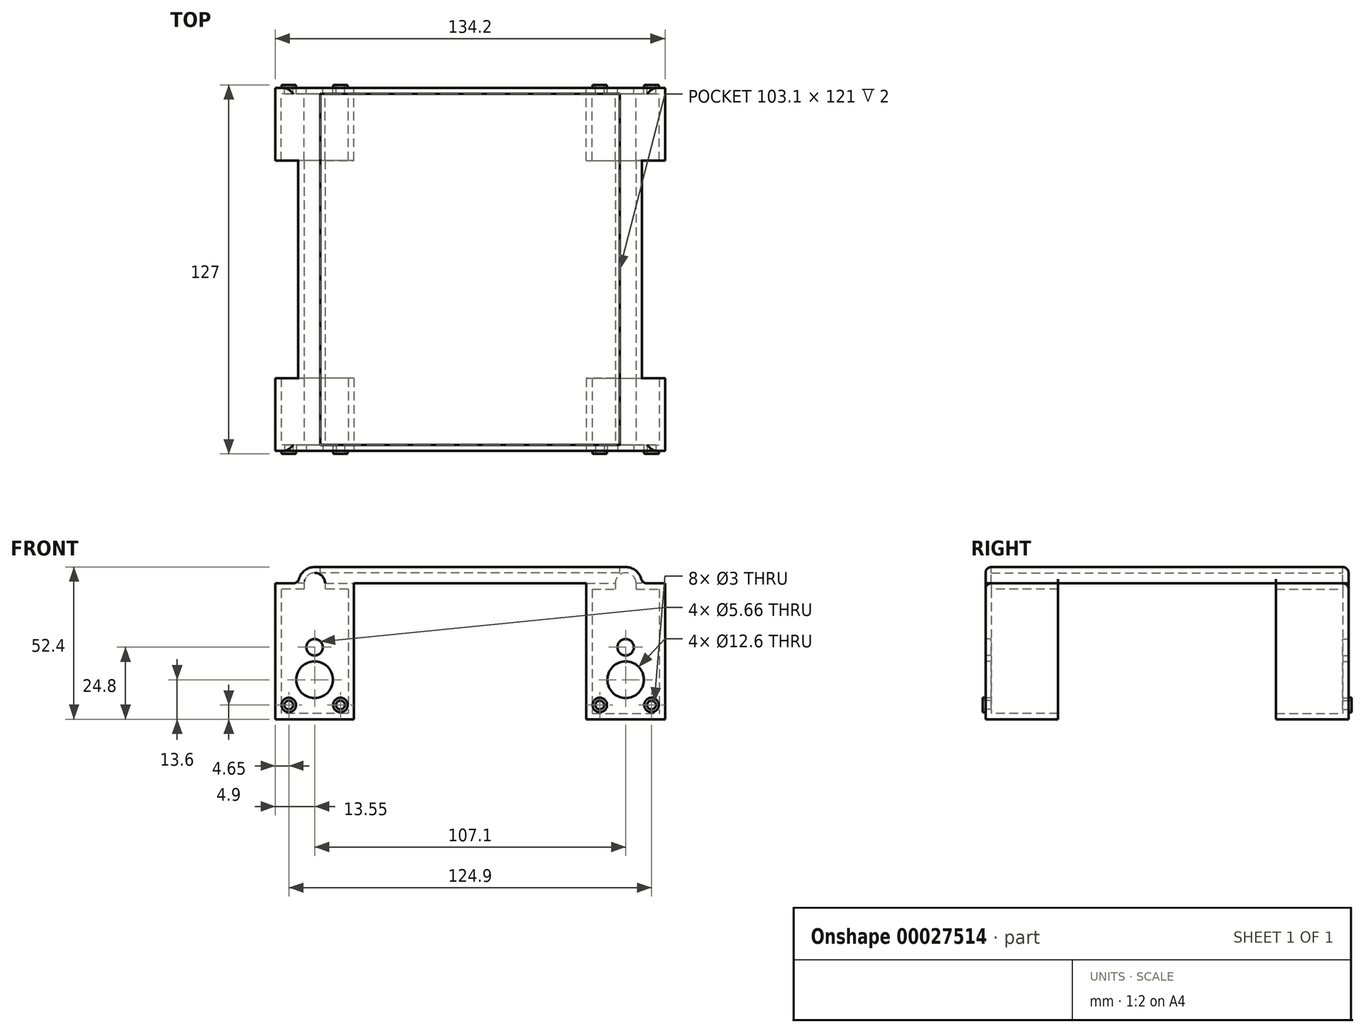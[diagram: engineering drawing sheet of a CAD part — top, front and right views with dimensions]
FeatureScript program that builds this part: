
annotation { "Feature Type Name" : "Feature", "Feature Type Description" : "" }
export const myFeature = defineFeature(function(context is Context, id is Id, definition is map)
    precondition{}
    {
        {
            assignVariable(context, id + "F0", {"name" : "FrameThickness", "anyValue" : 2});
        }
        {
            var Q0;
            Q0=qCreatedBy(makeId("Front.planeOp"),FACE);
            var sketch = newSketch(context, id + "F1", { "sketchPlane" : qUnion([Q0])});
            skLineSegment(sketch, "E0.rect.bottom", {"start": v(11.55, 21.4) * mm, "end": v(3.6, 21.4) * mm});
            skLineSegment(sketch, "E0.rect.top", {"start": v(11.55, -21.4) * mm, "end": v(-11.55, -21.4) * mm});
            skLineSegment(sketch, "E0.rect.left", {"start": v(11.55, 21.4) * mm, "end": v(11.55, -21.4) * mm});
            skLineSegment(sketch, "E0.rect.right", {"start": v(-11.55, 21.4) * mm, "end": v(-11.55, -21.4) * mm});
            skPoint(sketch, "E0.rect.middle", {"position": v(0, 0) * mm});
            skLineSegment(sketch, "E1.0", {"start": v(13.55, 23.4) * mm, "end": v(5.6, 23.4) * mm});
            skLineSegment(sketch, "E1.1", {"start": v(13.55, 23.4) * mm, "end": v(13.55, -23.4) * mm});
            skLineSegment(sketch, "E1.2", {"start": v(13.55, -23.4) * mm, "end": v(-13.55, -23.4) * mm});
            skLineSegment(sketch, "E1.3", {"start": v(-13.55, 23.4) * mm, "end": v(-13.55, -23.4) * mm});
            skCircle(sketch, "E2", {"center": v(0, -9.8) * mm, "radius": 6.3 * mm});
            skPoint(sketch, "E2.centerSnap0", {"position": v(0, -21.4) * mm});
            skLineSegment(sketch, "E3", {"start": v(0, -9.8) * mm, "end": v(0, -21.4) * mm, "construction": true});
            skCircle(sketch, "E4", {"center": v(8.9, -18.5) * mm, "radius": 1.5 * mm});
            skCircle(sketch, "E5", {"center": v(-8.9, -18.5) * mm, "radius": 1.5 * mm});
            skCircle(sketch, "E6", {"center": v(0, 1.4) * mm, "radius": 2.83 * mm});
            skLineSegment(sketch, "E7", {"start": v(0, 1.4) * mm, "end": v(0, -9.8) * mm, "construction": true});
            skLineSegment(sketch, "E8", {"start": v(-11.55, -9.8) * mm, "end": v(11.55, -9.8) * mm, "construction": true});
            skLineSegment(sketch, "E9", {"start": v(8.9, -18.5) * mm, "end": v(8.9, -9.8) * mm, "construction": true});
            skLineSegment(sketch, "E10", {"start": v(8.9, -18.5) * mm, "end": v(-8.9, -18.5) * mm, "construction": true});
            skArc(sketch, "E11", {"start": v(3.6, 23.4) * mm, "mid": v(0, 27) * mm, "end": v(-3.6, 23.4) * mm});
            skLineSegment(sketch, "E12", {"start": v(3.6, 23.4) * mm, "end": v(-3.6, 23.4) * mm, "construction": true});
            skLineSegment(sketch, "E13", {"start": v(0, 23.4) * mm, "end": v(0, 27) * mm, "construction": true});
            skArc(sketch, "E14.0", {"start": v(5.6, 23.4) * mm, "mid": v(3.96, 27.36) * mm, "end": v(0, 29) * mm, "construction": true});
            skLineSegment(sketch, "E15", {"start": v(-5.6, 23.4) * mm, "end": v(-13.55, 23.4) * mm});
            skLineSegment(sketch, "E16", {"start": v(-3.6, 23.4) * mm, "end": v(-3.6, 21.4) * mm});
            skLineSegment(sketch, "E17", {"start": v(3.6, 23.4) * mm, "end": v(3.6, 21.4) * mm});
            skLineSegment(sketch, "E18", {"start": v(-3.6, 21.4) * mm, "end": v(-11.55, 21.4) * mm});
            skLineSegment(sketch, "E19", {"start": v(3.6, 21.4) * mm, "end": v(-3.6, 21.4) * mm});
            skCircle(sketch, "E20.0", {"center": v(8.9, -18.5) * mm, "radius": 2.5 * mm});
            skLineSegment(sketch, "E21.0", {"start": v(8.9, -13.5) * mm, "end": v(-8.9, -13.5) * mm});
            skCircle(sketch, "E22.0", {"center": v(-8.9, -18.5) * mm, "radius": 2.5 * mm});
            skLineSegment(sketch, "E23", {"start": v(5.6, 23.4) * mm, "end": v(5.6, 29) * mm});
            skPoint(sketch, "E23.endSnap0", {"position": v(0, 29) * mm});
            skLineSegment(sketch, "E24", {"start": v(5.6, 29) * mm, "end": v(0, 29) * mm});
            skArc(sketch, "E25", {"start": v(0, 29) * mm, "mid": v(-3.96, 27.36) * mm, "end": v(-5.6, 23.4) * mm});
            skSolve(sketch);
        }
        {
            var Q0;
            Q0=makeQuery(id+"F1.imprint","IMPRINT",FACE,{"disambiguationData":[TD([[makeQuery(id+"F1.imprint","IMPRINT",EDGE,{"derivedFrom":sQuery(id+"F1.wireOp",EDGE,"E0.rect.bottom")}),1.0]])]});
            var Q1;
            Q1=makeQuery(id+"F1.imprint","IMPRINT",FACE,{"disambiguationData":[TD([[makeQuery(id+"F1.imprint","IMPRINT",EDGE,{"derivedFrom":sQuery(id+"F1.wireOp",EDGE,"E11")}),1.0]])]});
            var Q2;
            Q2=makeQuery(id+"F1.imprint","IMPRINT",FACE,{"disambiguationData":[TD([[makeQuery(id+"F1.imprint","IMPRINT",EDGE,{"derivedFrom":sQuery(id+"F1.wireOp",EDGE,"E5")}),-1.0]])]});
            var Q3;
            Q3=makeQuery(id+"F1.imprint","IMPRINT",FACE,{"disambiguationData":[TD([[makeQuery(id+"F1.imprint","IMPRINT",EDGE,{"derivedFrom":sQuery(id+"F1.wireOp",EDGE,"E4")}),-1.0]])]});
            extrude(context, id + "F2", {"entities" : qUnion([Q0, Q1, Q2, Q3]), "depth" : (getVariable(context, 'FrameThickness')) * mm});
        }
        {
            var Q0;
            Q0=makeQuery(id+"F1.imprint","IMPRINT",FACE,{"disambiguationData":[TD([[makeQuery(id+"F1.imprint","IMPRINT",EDGE,{"derivedFrom":sQuery(id+"F1.wireOp",EDGE,"E5")}),-1.0]])]});
            var Q1;
            Q1=makeQuery(id+"F1.imprint","IMPRINT",FACE,{"disambiguationData":[TD([[makeQuery(id+"F1.imprint","IMPRINT",EDGE,{"derivedFrom":sQuery(id+"F1.wireOp",EDGE,"E4")}),-1.0]])]});
            extrude(context, id + "F3", {"entities" : qUnion([Q0, Q1]), "operationType" : NewBodyOperationType.ADD, "oppositeDirection" : true, "depth" : 1 * mm});
        }
        {
            var Q0;
            Q0=makeQuery(id+"F1.imprint","IMPRINT",FACE,{"disambiguationData":[TD([[makeQuery(id+"F1.imprint","IMPRINT",EDGE,{"derivedFrom":sQuery(id+"F1.wireOp",EDGE,"E0.rect.bottom")}),-1.0]])]});
            extrude(context, id + "F4", {"entities" : qUnion([Q0]), "operationType" : NewBodyOperationType.ADD, "depth" : 25 * mm});
        }
        {
            var Q0;
            {var subQ0=sQuery(id+"F1.wireOp",EDGE,"E1.0");var subQ1=sQuery(id+"F1.wireOp",EDGE,"E23");var subQ2=makeQuery(id+"F4.opExtrude","CAP_VERTEX",VERTEX,{"disambiguationData":[OSD([subQ0,subQ1])],"isStart":true});Q0=makeQuery(id+"F11.opLoft","SWEPT_EDGE",EDGE,{"disambiguationData":[OSD([subQ0,subQ1]),TDD([subQ2,makeQuery(id+"F8.opPattern","COPY",VERTEX,{"derivedFrom":subQ2,"instanceName":"1"})])]});}
            var Q1;
            {var subQ0=sQuery(id+"F1.wireOp",EDGE,"E24");var subQ1=makeQuery(id+"F4.opExtrude","CAP_EDGE",EDGE,{"disambiguationData":[OSD([subQ0])],"isStart":true});var subQ2=sQuery(id+"F1.wireOp",EDGE,"E23");var subQ3=makeQuery(id+"F4.opExtrude","CAP_VERTEX",VERTEX,{"disambiguationData":[OSD([subQ2,subQ0])],"isStart":true});Q1=makeQuery(id+"F11.boolean.opBoolean","MERGE",EDGE,{"derivedFrom":[subQ1,makeQuery(id+"F8.opPattern","COPY",EDGE,{"derivedFrom":subQ1,"instanceName":"1"}),makeQuery(id+"F11.opLoft","SWEPT_EDGE",EDGE,{"disambiguationData":[OSD([subQ2,subQ0]),TDD([subQ3,makeQuery(id+"F8.opPattern","COPY",VERTEX,{"derivedFrom":subQ3,"instanceName":"1"})])]})]});}
            var Q2;
            Q2=makeQuery(id+"F8.opPattern","COPY",EDGE,{"derivedFrom":makeQuery(id+"F4.opExtrude","SWEPT_EDGE",EDGE,{"disambiguationData":[OSD([sQuery(id+"F1.wireOp",EDGE,"E15"),sQuery(id+"F1.wireOp",EDGE,"E25")])]}),"instanceName":"1"});
            var Q3;
            Q3=makeQuery(id+"F8.opPattern","COPY",EDGE,{"derivedFrom":makeQuery(id+"F6.opPattern","COPY",EDGE,{"derivedFrom":makeQuery(id+"F4.opExtrude","SWEPT_EDGE",EDGE,{"disambiguationData":[OSD([sQuery(id+"F1.wireOp",EDGE,"E15"),sQuery(id+"F1.wireOp",EDGE,"E25")])]}),"instanceName":"1"}),"instanceName":"1"});
            var Q4;
            {var subQ0=sQuery(id+"F1.wireOp",EDGE,"E1.0");var subQ1=sQuery(id+"F1.wireOp",EDGE,"E23");var subQ2=makeQuery(id+"F6.opPattern","COPY",VERTEX,{"derivedFrom":makeQuery(id+"F4.opExtrude","CAP_VERTEX",VERTEX,{"disambiguationData":[OSD([subQ0,subQ1])],"isStart":true}),"instanceName":"1"});Q4=makeQuery(id+"F10.opLoft","SWEPT_EDGE",EDGE,{"disambiguationData":[OSD([subQ0,subQ1]),TDD([subQ2,makeQuery(id+"F8.opPattern","COPY",VERTEX,{"derivedFrom":subQ2,"instanceName":"1"})])]});}
            var Q5;
            {var subQ0=sQuery(id+"F1.wireOp",EDGE,"E24");var subQ1=makeQuery(id+"F6.opPattern","COPY",EDGE,{"derivedFrom":makeQuery(id+"F4.opExtrude","CAP_EDGE",EDGE,{"disambiguationData":[OSD([subQ0])],"isStart":true}),"instanceName":"1"});var subQ2=sQuery(id+"F1.wireOp",EDGE,"E23");var subQ3=makeQuery(id+"F6.opPattern","COPY",VERTEX,{"derivedFrom":makeQuery(id+"F4.opExtrude","CAP_VERTEX",VERTEX,{"disambiguationData":[OSD([subQ2,subQ0])],"isStart":true}),"instanceName":"1"});Q5=makeQuery(id+"F10.boolean.opBoolean","MERGE",EDGE,{"derivedFrom":[subQ1,makeQuery(id+"F8.opPattern","COPY",EDGE,{"derivedFrom":subQ1,"instanceName":"1"}),makeQuery(id+"F10.opLoft","SWEPT_EDGE",EDGE,{"disambiguationData":[OSD([subQ2,subQ0]),TDD([subQ3,makeQuery(id+"F8.opPattern","COPY",VERTEX,{"derivedFrom":subQ3,"instanceName":"1"})])]})]});}
            var Q6;
            Q6=makeQuery(id+"F6.opPattern","COPY",EDGE,{"derivedFrom":makeQuery(id+"F4.opExtrude","SWEPT_EDGE",EDGE,{"disambiguationData":[OSD([sQuery(id+"F1.wireOp",EDGE,"E15"),sQuery(id+"F1.wireOp",EDGE,"E25")])]}),"instanceName":"1"});
            var Q7;
            Q7=makeQuery(id+"F4.opExtrude","SWEPT_EDGE",EDGE,{"disambiguationData":[OSD([sQuery(id+"F1.wireOp",EDGE,"E15"),sQuery(id+"F1.wireOp",EDGE,"E25")])]});
            fillet(context, id + "F5", {"entities" : qUnion([Q0, Q1, Q2, Q3, Q4, Q5, Q6, Q7]), "radius" : 2 * mm, "tangentPropagation" : true, "allowEdgeOverflow" : false});
        }
        {
            var Q0;
            Q0=makeQuery(id+"F2.opExtrude","SWEPT_BODY",BODY,{"disambiguationData":[OSD([sQuery(id+"F1.wireOp",EDGE,"E0.rect.bottom"),sQuery(id+"F1.wireOp",EDGE,"E0.rect.top"),sQuery(id+"F1.wireOp",EDGE,"E0.rect.left"),sQuery(id+"F1.wireOp",EDGE,"E0.rect.right"),sQuery(id+"F1.wireOp",EDGE,"E2"),sQuery(id+"F1.wireOp",EDGE,"E4"),sQuery(id+"F1.wireOp",EDGE,"E5"),sQuery(id+"F1.wireOp",EDGE,"E6"),sQuery(id+"F1.wireOp",EDGE,"E11"),sQuery(id+"F1.wireOp",EDGE,"E16"),sQuery(id+"F1.wireOp",EDGE,"E17"),sQuery(id+"F1.wireOp",EDGE,"E18")])]});
            var Q1;
            Q1=makeQuery(id+"F4.opExtrude","CAP_FACE",FACE,{"disambiguationData":[OSD([sQuery(id+"F1.wireOp",EDGE,"E0.rect.bottom"),sQuery(id+"F1.wireOp",EDGE,"E0.rect.top"),sQuery(id+"F1.wireOp",EDGE,"E0.rect.left"),sQuery(id+"F1.wireOp",EDGE,"E0.rect.right"),sQuery(id+"F1.wireOp",EDGE,"E1.0"),sQuery(id+"F1.wireOp",EDGE,"E1.1"),sQuery(id+"F1.wireOp",EDGE,"E1.2"),sQuery(id+"F1.wireOp",EDGE,"E1.3"),sQuery(id+"F1.wireOp",EDGE,"E11"),sQuery(id+"F1.wireOp",EDGE,"E14.0"),sQuery(id+"F1.wireOp",EDGE,"E15"),sQuery(id+"F1.wireOp",EDGE,"E16"),sQuery(id+"F1.wireOp",EDGE,"E17"),sQuery(id+"F1.wireOp",EDGE,"E18")])],"isStart":false});
            mirror(context, id + "F6", {"entities" : qUnion([Q0]), "mirrorPlane" : qUnion([Q1])});
        }
        {
            var Q0;
            Q0=makeQuery(id+"F6.opPattern","COPY",BODY,{"derivedFrom":makeQuery(id+"F2.opExtrude","SWEPT_BODY",BODY,{"disambiguationData":[OSD([sQuery(id+"F1.wireOp",EDGE,"E0.rect.bottom"),sQuery(id+"F1.wireOp",EDGE,"E0.rect.top"),sQuery(id+"F1.wireOp",EDGE,"E0.rect.left"),sQuery(id+"F1.wireOp",EDGE,"E0.rect.right"),sQuery(id+"F1.wireOp",EDGE,"E2"),sQuery(id+"F1.wireOp",EDGE,"E4"),sQuery(id+"F1.wireOp",EDGE,"E5"),sQuery(id+"F1.wireOp",EDGE,"E6"),sQuery(id+"F1.wireOp",EDGE,"E11"),sQuery(id+"F1.wireOp",EDGE,"E16"),sQuery(id+"F1.wireOp",EDGE,"E17"),sQuery(id+"F1.wireOp",EDGE,"E18")])]}),"instanceName":"1"});
            var Q1;
            Q1=makeQuery(id+"F4.opExtrude","SWEPT_EDGE",EDGE,{"disambiguationData":[OSD([sQuery(id+"F1.wireOp",EDGE,"E1.0"),sQuery(id+"F1.wireOp",EDGE,"E1.1")])]});
            transform(context, id + "F7", {"entities" : qUnion([Q0]), "transformType" : TransformType.TRANSLATION_DISTANCE, "transformDirection" : qUnion([Q1]), "distance" : 75 * mm, "oppositeDirection" : true, "makeCopy" : false});
        }
        {
            var Q0;
            Q0=makeQuery(id+"F2.opExtrude","SWEPT_BODY",BODY,{"disambiguationData":[OSD([sQuery(id+"F1.wireOp",EDGE,"E0.rect.bottom"),sQuery(id+"F1.wireOp",EDGE,"E0.rect.top"),sQuery(id+"F1.wireOp",EDGE,"E0.rect.left"),sQuery(id+"F1.wireOp",EDGE,"E0.rect.right"),sQuery(id+"F1.wireOp",EDGE,"E2"),sQuery(id+"F1.wireOp",EDGE,"E4"),sQuery(id+"F1.wireOp",EDGE,"E5"),sQuery(id+"F1.wireOp",EDGE,"E6"),sQuery(id+"F1.wireOp",EDGE,"E11"),sQuery(id+"F1.wireOp",EDGE,"E16"),sQuery(id+"F1.wireOp",EDGE,"E17"),sQuery(id+"F1.wireOp",EDGE,"E18")])]});
            var Q1;
            Q1=makeQuery(id+"F6.opPattern","COPY",BODY,{"derivedFrom":makeQuery(id+"F2.opExtrude","SWEPT_BODY",BODY,{"disambiguationData":[OSD([sQuery(id+"F1.wireOp",EDGE,"E0.rect.bottom"),sQuery(id+"F1.wireOp",EDGE,"E0.rect.top"),sQuery(id+"F1.wireOp",EDGE,"E0.rect.left"),sQuery(id+"F1.wireOp",EDGE,"E0.rect.right"),sQuery(id+"F1.wireOp",EDGE,"E2"),sQuery(id+"F1.wireOp",EDGE,"E4"),sQuery(id+"F1.wireOp",EDGE,"E5"),sQuery(id+"F1.wireOp",EDGE,"E6"),sQuery(id+"F1.wireOp",EDGE,"E11"),sQuery(id+"F1.wireOp",EDGE,"E16"),sQuery(id+"F1.wireOp",EDGE,"E17"),sQuery(id+"F1.wireOp",EDGE,"E18")])]}),"instanceName":"1"});
            var Q2;
            Q2=makeQuery(id+"F6.opPattern","COPY",FACE,{"derivedFrom":makeQuery(id+"F4.opExtrude","SWEPT_FACE",FACE,{"disambiguationData":[OSD([sQuery(id+"F1.wireOp",EDGE,"E1.1")])]}),"instanceName":"1"});
            mirror(context, id + "F8", {"entities" : qUnion([Q0, Q1]), "mirrorPlane" : qUnion([Q2])});
        }
        {
            var Q0;
            Q0=makeQuery(id+"F8.opPattern","COPY",BODY,{"derivedFrom":makeQuery(id+"F6.opPattern","COPY",BODY,{"derivedFrom":makeQuery(id+"F2.opExtrude","SWEPT_BODY",BODY,{"disambiguationData":[OSD([sQuery(id+"F1.wireOp",EDGE,"E0.rect.bottom"),sQuery(id+"F1.wireOp",EDGE,"E0.rect.top"),sQuery(id+"F1.wireOp",EDGE,"E0.rect.left"),sQuery(id+"F1.wireOp",EDGE,"E0.rect.right"),sQuery(id+"F1.wireOp",EDGE,"E2"),sQuery(id+"F1.wireOp",EDGE,"E4"),sQuery(id+"F1.wireOp",EDGE,"E5"),sQuery(id+"F1.wireOp",EDGE,"E6"),sQuery(id+"F1.wireOp",EDGE,"E11"),sQuery(id+"F1.wireOp",EDGE,"E16"),sQuery(id+"F1.wireOp",EDGE,"E17"),sQuery(id+"F1.wireOp",EDGE,"E18")])]}),"instanceName":"1"}),"instanceName":"1"});
            var Q1;
            Q1=makeQuery(id+"F8.opPattern","COPY",BODY,{"derivedFrom":makeQuery(id+"F2.opExtrude","SWEPT_BODY",BODY,{"disambiguationData":[OSD([sQuery(id+"F1.wireOp",EDGE,"E0.rect.bottom"),sQuery(id+"F1.wireOp",EDGE,"E0.rect.top"),sQuery(id+"F1.wireOp",EDGE,"E0.rect.left"),sQuery(id+"F1.wireOp",EDGE,"E0.rect.right"),sQuery(id+"F1.wireOp",EDGE,"E2"),sQuery(id+"F1.wireOp",EDGE,"E4"),sQuery(id+"F1.wireOp",EDGE,"E5"),sQuery(id+"F1.wireOp",EDGE,"E6"),sQuery(id+"F1.wireOp",EDGE,"E11"),sQuery(id+"F1.wireOp",EDGE,"E16"),sQuery(id+"F1.wireOp",EDGE,"E17"),sQuery(id+"F1.wireOp",EDGE,"E18")])]}),"instanceName":"1"});
            var Q2;
            Q2=makeQuery(id+"F6.opPattern","COPY",EDGE,{"derivedFrom":makeQuery(id+"F4.opExtrude","CAP_EDGE",EDGE,{"disambiguationData":[OSD([sQuery(id+"F1.wireOp",EDGE,"E1.0")])],"isStart":false}),"instanceName":"1"});
            var Q3;
            Q3=makeQuery(id+"F6.opPattern","COPY",EDGE,{"derivedFrom":makeQuery(id+"F4.opExtrude","CAP_EDGE",EDGE,{"disambiguationData":[OSD([sQuery(id+"F1.wireOp",EDGE,"E1.0")])],"isStart":false}),"instanceName":"1"});
            transform(context, id + "F9", {"entities" : qUnion([Q0, Q1]), "transformType" : TransformType.TRANSLATION_DISTANCE, "transformDirection" : qUnion([Q3]), "distance" : 80 * mm, "oppositeDirection" : true, "makeCopy" : false});
        }
        {
            var Q0;
            Q0=makeQuery(id+"F8.opPattern","COPY",FACE,{"derivedFrom":makeQuery(id+"F6.opPattern","COPY",FACE,{"derivedFrom":makeQuery(id+"F4.opExtrude","SWEPT_FACE",FACE,{"disambiguationData":[OSD([sQuery(id+"F1.wireOp",EDGE,"E23")])]}),"instanceName":"1"}),"instanceName":"1"});
            var Q1;
            Q1=makeQuery(id+"F6.opPattern","COPY",FACE,{"derivedFrom":makeQuery(id+"F4.opExtrude","SWEPT_FACE",FACE,{"disambiguationData":[OSD([sQuery(id+"F1.wireOp",EDGE,"E23")])]}),"instanceName":"1"});
            loft(context, id + "F10", {"operationType" : NewBodyOperationType.ADD, "sheetProfilesArray" : [{ "sheetProfileEntities" : qUnion([Q0]) }, { "sheetProfileEntities" : qUnion([Q1]) }]});
        }
        {
            var Q0;
            Q0=makeQuery(id+"F8.opPattern","COPY",FACE,{"derivedFrom":makeQuery(id+"F4.opExtrude","SWEPT_FACE",FACE,{"disambiguationData":[OSD([sQuery(id+"F1.wireOp",EDGE,"E23")])]}),"instanceName":"1"});
            var Q1;
            Q1=makeQuery(id+"F4.opExtrude","SWEPT_FACE",FACE,{"disambiguationData":[OSD([sQuery(id+"F1.wireOp",EDGE,"E23")])]});
            loft(context, id + "F11", {"operationType" : NewBodyOperationType.ADD, "sheetProfilesArray" : [{ "sheetProfileEntities" : qUnion([Q0]) }, { "sheetProfileEntities" : qUnion([Q1]) }]});
        }
        {
            var Q0;
            {var subQ0=sQuery(id+"F1.wireOp",EDGE,"E1.0");var subQ1=sQuery(id+"F1.wireOp",EDGE,"E23");var subQ2=sQuery(id+"F1.wireOp",EDGE,"E24");var subQ3=makeQuery(id+"F6.opPattern","COPY",FACE,{"derivedFrom":makeQuery(id+"F4.opExtrude","CAP_FACE",FACE,{"disambiguationData":[OSD([sQuery(id+"F1.wireOp",EDGE,"E0.rect.bottom"),sQuery(id+"F1.wireOp",EDGE,"E0.rect.top"),sQuery(id+"F1.wireOp",EDGE,"E0.rect.left"),sQuery(id+"F1.wireOp",EDGE,"E0.rect.right"),subQ0,sQuery(id+"F1.wireOp",EDGE,"E1.1"),sQuery(id+"F1.wireOp",EDGE,"E1.2"),sQuery(id+"F1.wireOp",EDGE,"E1.3"),sQuery(id+"F1.wireOp",EDGE,"E11"),sQuery(id+"F1.wireOp",EDGE,"E15"),sQuery(id+"F1.wireOp",EDGE,"E16"),sQuery(id+"F1.wireOp",EDGE,"E17"),sQuery(id+"F1.wireOp",EDGE,"E18"),subQ1,subQ2,sQuery(id+"F1.wireOp",EDGE,"E25")])],"isStart":false}),"instanceName":"1"});var subQ4=makeQuery(id+"F6.opPattern","COPY",VERTEX,{"derivedFrom":makeQuery(id+"F4.opExtrude","CAP_VERTEX",VERTEX,{"disambiguationData":[OSD([subQ0,subQ1])],"isStart":false}),"instanceName":"1"});var subQ5=makeQuery(id+"F6.opPattern","COPY",VERTEX,{"derivedFrom":makeQuery(id+"F4.opExtrude","CAP_VERTEX",VERTEX,{"disambiguationData":[OSD([subQ1,subQ2])],"isStart":false}),"instanceName":"1"});var subQ6=makeQuery(id+"F6.opPattern","COPY",EDGE,{"derivedFrom":makeQuery(id+"F4.opExtrude","CAP_EDGE",EDGE,{"disambiguationData":[OSD([subQ1])],"isStart":false}),"instanceName":"1"});Q0=makeQuery(id+"F10.boolean.opBoolean","MERGE",FACE,{"derivedFrom":[subQ3,makeQuery(id+"F8.opPattern","COPY",FACE,{"derivedFrom":subQ3,"instanceName":"1"}),makeQuery(id+"F10.opLoft","SWEPT_FACE",FACE,{"disambiguationData":[OSD([subQ0,subQ1,subQ2]),TDD([subQ4,subQ5,subQ6,makeQuery(id+"F8.opPattern","COPY",VERTEX,{"derivedFrom":subQ4,"instanceName":"1"}),makeQuery(id+"F8.opPattern","COPY",VERTEX,{"derivedFrom":subQ5,"instanceName":"1"}),makeQuery(id+"F8.opPattern","COPY",EDGE,{"derivedFrom":subQ6,"instanceName":"1"})])]})]});}
            var sketch = newSketch(context, id + "F12", { "sketchPlane" : qUnion([Q0])});
            skLineSegment(sketch, "E26", {"start": v(-13.55, 23.4) * mm, "end": v(-3.6, 23.4) * mm});
            skLineSegment(sketch, "E27", {"start": v(-93.55, 23.4) * mm, "end": v(-103.5, 23.4) * mm});
            skArc(sketch, "E28.0", {"start": v(-103.5, 23.4) * mm, "mid": v(-107.1, 27) * mm, "end": v(-110.7, 23.4) * mm});
            skArc(sketch, "E29.0", {"start": v(-107.1, 29) * mm, "mid": v(-111.06, 27.36) * mm, "end": v(-112.7, 23.4) * mm});
            skLineSegment(sketch, "E30.0", {"start": v(-107.1, 29) * mm, "end": v(0, 29) * mm});
            skArc(sketch, "E31.0", {"start": v(0, 29) * mm, "mid": v(3.96, 27.36) * mm, "end": v(5.6, 23.4) * mm});
            skLineSegment(sketch, "E32.0", {"start": v(-93.55, 23.4) * mm, "end": v(-13.55, 23.4) * mm});
            skLineSegment(sketch, "E33", {"start": v(-110.7, 23.4) * mm, "end": v(-112.7, 23.4) * mm});
            skLineSegment(sketch, "E34", {"start": v(5.6, 23.4) * mm, "end": v(3.6, 23.4) * mm});
            skSolve(sketch);
        }
        {
            var Q0;
            Q0=makeQuery(id+"F12.imprint","IMPRINT",FACE,{"disambiguationData":[TD([[makeQuery(id+"F12.imprint","IMPRINT",EDGE,{"derivedFrom":sQuery(id+"F12.wireOp",EDGE,"E26")}),1.0]])]});
            var Q1;
            {var subQ0=sQuery(id+"F1.wireOp",EDGE,"E1.0");var subQ1=sQuery(id+"F1.wireOp",EDGE,"E23");var subQ2=sQuery(id+"F1.wireOp",EDGE,"E24");var subQ3=makeQuery(id+"F4.opExtrude","CAP_FACE",FACE,{"disambiguationData":[OSD([sQuery(id+"F1.wireOp",EDGE,"E0.rect.bottom"),sQuery(id+"F1.wireOp",EDGE,"E0.rect.top"),sQuery(id+"F1.wireOp",EDGE,"E0.rect.left"),sQuery(id+"F1.wireOp",EDGE,"E0.rect.right"),subQ0,sQuery(id+"F1.wireOp",EDGE,"E1.1"),sQuery(id+"F1.wireOp",EDGE,"E1.2"),sQuery(id+"F1.wireOp",EDGE,"E1.3"),sQuery(id+"F1.wireOp",EDGE,"E11"),sQuery(id+"F1.wireOp",EDGE,"E15"),sQuery(id+"F1.wireOp",EDGE,"E16"),sQuery(id+"F1.wireOp",EDGE,"E17"),sQuery(id+"F1.wireOp",EDGE,"E18"),subQ1,subQ2,sQuery(id+"F1.wireOp",EDGE,"E25")])],"isStart":false});var subQ4=makeQuery(id+"F4.opExtrude","CAP_VERTEX",VERTEX,{"disambiguationData":[OSD([subQ0,subQ1])],"isStart":false});var subQ5=makeQuery(id+"F4.opExtrude","CAP_VERTEX",VERTEX,{"disambiguationData":[OSD([subQ1,subQ2])],"isStart":false});var subQ6=makeQuery(id+"F4.opExtrude","CAP_EDGE",EDGE,{"disambiguationData":[OSD([subQ1])],"isStart":false});Q1=makeQuery(id+"F11.boolean.opBoolean","MERGE",FACE,{"derivedFrom":[subQ3,makeQuery(id+"F8.opPattern","COPY",FACE,{"derivedFrom":subQ3,"instanceName":"1"}),makeQuery(id+"F11.opLoft","SWEPT_FACE",FACE,{"disambiguationData":[OSD([subQ0,subQ1,subQ2]),TDD([subQ4,subQ5,subQ6,makeQuery(id+"F8.opPattern","COPY",VERTEX,{"derivedFrom":subQ4,"instanceName":"1"}),makeQuery(id+"F8.opPattern","COPY",VERTEX,{"derivedFrom":subQ5,"instanceName":"1"}),makeQuery(id+"F8.opPattern","COPY",EDGE,{"derivedFrom":subQ6,"instanceName":"1"})])]})]});}
            extrude(context, id + "F13", {"entities" : qUnion([Q0]), "operationType" : NewBodyOperationType.ADD, "endBound" : BoundingType.UP_TO_SURFACE, "endBoundEntityFace" : qUnion([Q1]), "depth" : 25 * mm});
        }
        {
            var Q0;
            {var subQ0=sQuery(id+"F1.wireOp",EDGE,"E24");var subQ1=makeQuery(id+"F4.opExtrude","SWEPT_FACE",FACE,{"disambiguationData":[OSD([subQ0])]});var subQ2=makeQuery(id+"F6.opPattern","COPY",FACE,{"derivedFrom":subQ1,"instanceName":"1"});var subQ3=sQuery(id+"F1.wireOp",EDGE,"E23");Q0=makeQuery(id+"F13.boolean.opBoolean","MERGE",FACE,{"derivedFrom":[makeQuery(id+"F10.boolean.opBoolean","MERGE",FACE,{"derivedFrom":[subQ2,makeQuery(id+"F8.opPattern","COPY",FACE,{"derivedFrom":subQ2,"instanceName":"1"}),makeQuery(id+"F10.opLoft","SWEPT_FACE",FACE,{"disambiguationData":[OSD([subQ3,subQ0])]})]}),makeQuery(id+"F11.boolean.opBoolean","MERGE",FACE,{"derivedFrom":[subQ1,makeQuery(id+"F8.opPattern","COPY",FACE,{"derivedFrom":subQ1,"instanceName":"1"}),makeQuery(id+"F11.opLoft","SWEPT_FACE",FACE,{"disambiguationData":[OSD([subQ3,subQ0])]})]}),makeQuery(id+"F13.opExtrude","SWEPT_FACE",FACE,{"disambiguationData":[OSD([sQuery(id+"F12.wireOp",EDGE,"E30.0")])]})]});}
            var sketch = newSketch(context, id + "F14", { "sketchPlane" : qUnion([Q0])});
            skLineSegment(sketch, "E35.0", {"start": v(2, -123) * mm, "end": v(2, -2) * mm});
            skLineSegment(sketch, "E35.1", {"start": v(105.1, -123) * mm, "end": v(2, -123) * mm});
            skLineSegment(sketch, "E35.2", {"start": v(105.1, -123) * mm, "end": v(105.1, -2) * mm});
            skLineSegment(sketch, "E35.3", {"start": v(105.1, -2) * mm, "end": v(2, -2) * mm});
            skSolve(sketch);
        }
        {
            var Q0;
            Q0=makeQuery(id+"F14.imprint","IMPRINT",FACE,{"disambiguationData":[TD([[makeQuery(id+"F14.imprint","IMPRINT",EDGE,{"derivedFrom":sQuery(id+"F14.wireOp",EDGE,"E35.0")}),-1.0]])]});
            extrude(context, id + "F15", {"entities" : qUnion([Q0]), "operationType" : NewBodyOperationType.REMOVE, "oppositeDirection" : true, "depth" : 2 * mm});
        }
    });
